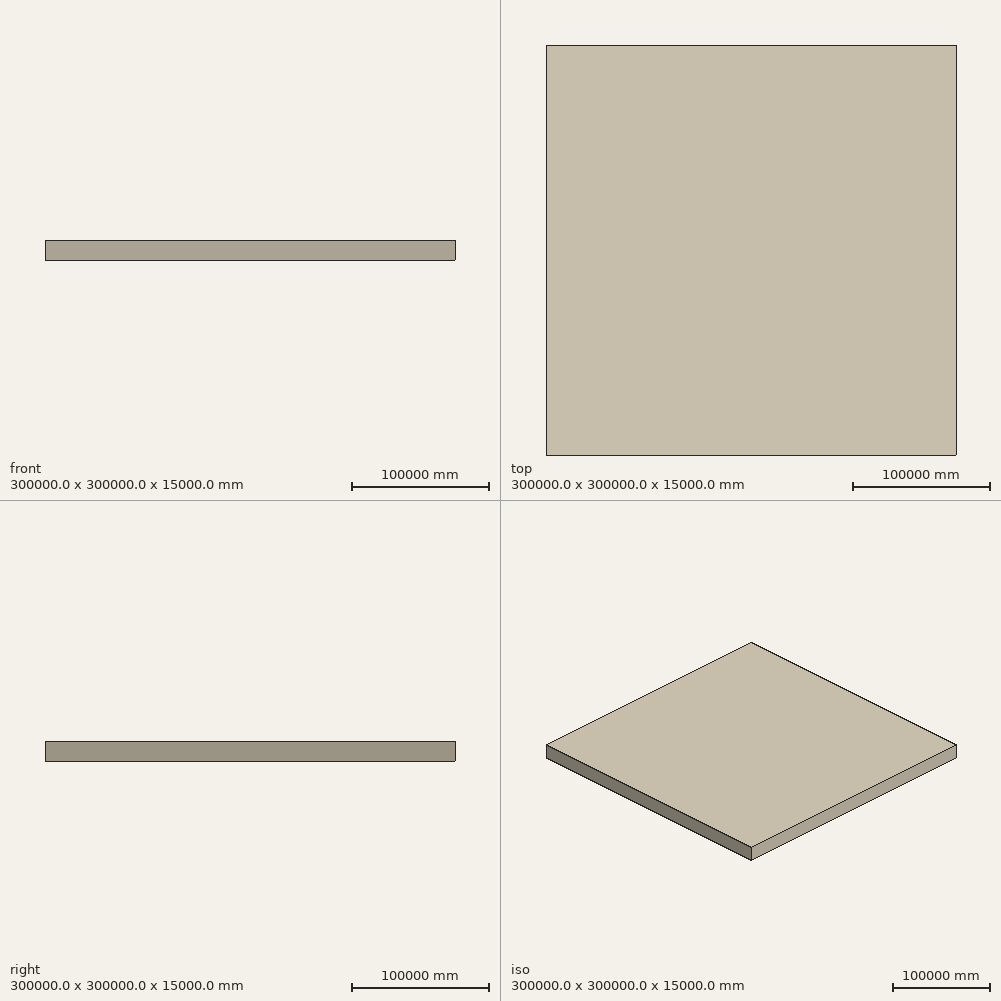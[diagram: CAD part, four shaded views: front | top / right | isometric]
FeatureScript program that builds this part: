
annotation { "Feature Type Name" : "Feature", "Feature Type Description" : "" }
export const myFeature = defineFeature(function(context is Context, id is Id, definition is map)
    precondition{}
    {
        {
            var Q0;
            Q0=qCreatedBy(makeId("Top.planeOp"),FACE);
            var sketch = newSketch(context, id + "F0", { "sketchPlane" : qUnion([Q0])});
            skLineSegment(sketch, "E0.bottom", {"start": v(0, 0) * mm, "end": v(300000, 0) * mm});
            skLineSegment(sketch, "E0.top", {"start": v(0, 300000) * mm, "end": v(300000, 300000) * mm});
            skLineSegment(sketch, "E0.left", {"start": v(0, 0) * mm, "end": v(0, 300000) * mm});
            skLineSegment(sketch, "E0.right", {"start": v(300000, 0) * mm, "end": v(300000, 300000) * mm});
            skSolve(sketch);
        }
        {
            var Q0;
            Q0=makeQuery(id+"F0.imprint","IMPRINT",FACE,{"disambiguationData":[TD([[makeQuery(id+"F0.imprint","IMPRINT",EDGE,{"derivedFrom":sQuery(id+"F0.wireOp",EDGE,"E0.bottom")}),1.0]])]});
            extrude(context, id + "F1", {"entities" : qUnion([Q0]), "oppositeDirection" : true, "depth" : 15000 * mm, "offsetDistance" : 25.4 * mm});
        }
    });
